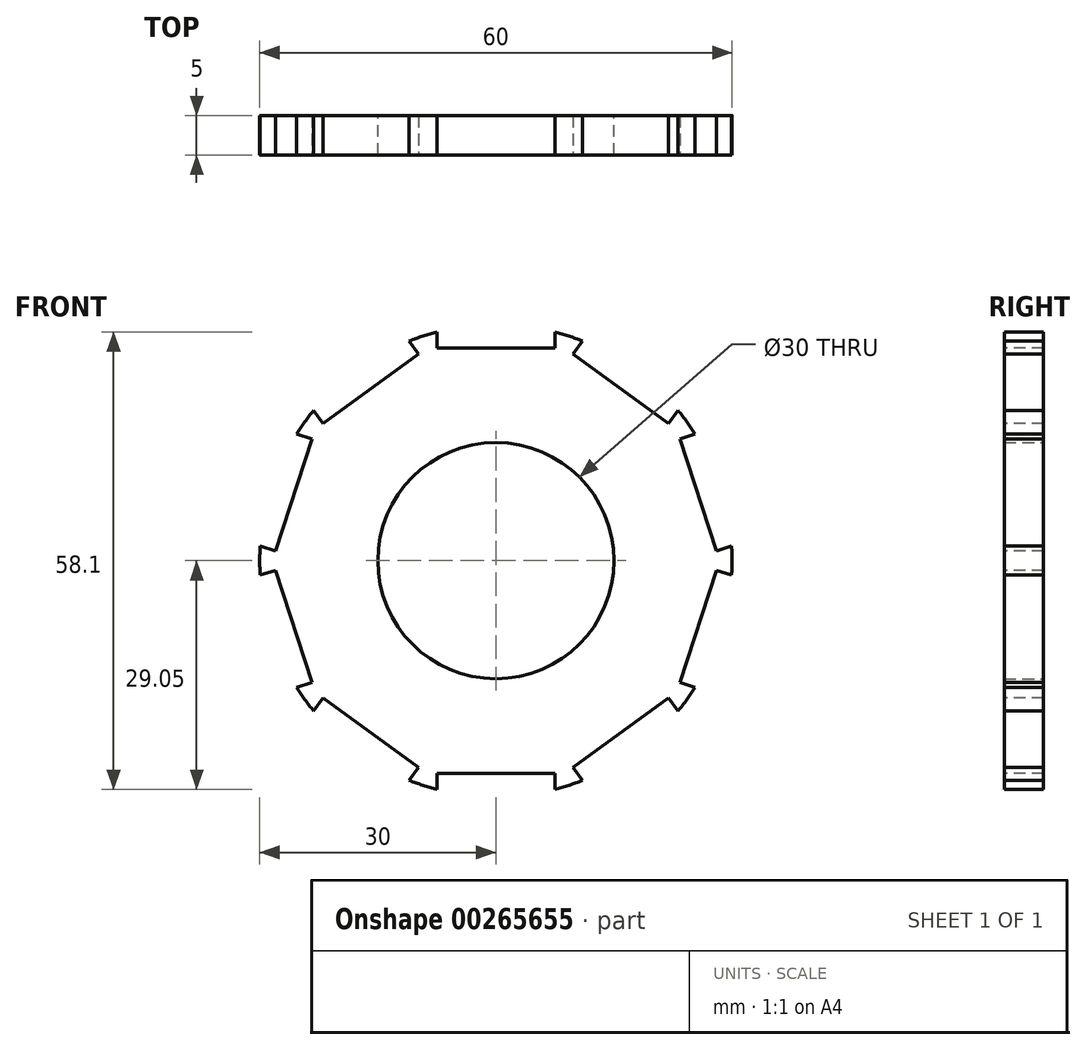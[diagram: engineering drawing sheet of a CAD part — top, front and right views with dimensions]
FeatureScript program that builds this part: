
annotation { "Feature Type Name" : "Feature", "Feature Type Description" : "" }
export const myFeature = defineFeature(function(context is Context, id is Id, definition is map)
    precondition{}
    {
        {
            var Q0;
            Q0=qCreatedBy(makeId("Front.planeOp"),FACE);
            var sketch = newSketch(context, id + "F0", { "sketchPlane" : qUnion([Q0])});
            skCircle(sketch, "E0", {"center": v(0, 0) * mm, "radius": 30 * mm});
            skCircle(sketch, "E1", {"center": v(0, 0) * mm, "radius": 15 * mm});
            skSolve(sketch);
        }
        {
            var Q0;
            Q0 = qSketchRegion(id + "F0", true);
            extrude(context, id + "F1", {"entities" : qUnion([Q0]), "depth" : 5 * mm});
        }
        {
            var Q0;
            Q0=makeQuery(id+"F1.opExtrude","CAP_FACE",FACE,{"disambiguationData":[OSD([sQuery(id+"F0.wireOp",EDGE,"E0"),sQuery(id+"F0.wireOp",EDGE,"E1")])],"isStart":false});
            var sketch = newSketch(context, id + "F3", { "sketchPlane" : qUnion([Q0])});
            skLineSegment(sketch, "E2", {"start": v(0, 30) * mm, "end": v(0, 27) * mm});
            skLineSegment(sketch, "E3", {"start": v(0, 27) * mm, "end": v(-7.5, 27) * mm});
            skLineSegment(sketch, "E4", {"start": v(-7.5, 27) * mm, "end": v(-7.5, 29.05) * mm});
            skLineSegment(sketch, "E5.MirrorCS", {"start": v(0, 27) * mm, "end": v(7.5, 27) * mm});
            skLineSegment(sketch, "E6.MirrorCS", {"start": v(7.5, 27) * mm, "end": v(7.5, 29.05) * mm});
            skArc(sketch, "E7", {"start": v(7.5, 29.05) * mm, "mid": v(0, 30) * mm, "end": v(-7.5, 29.05) * mm});
            skLineSegment(sketch, "E8.1.0", {"start": v(-15.87, 21.84) * mm, "end": v(-21.94, 17.44) * mm});
            skLineSegment(sketch, "E8.1.1", {"start": v(-15.87, 21.84) * mm, "end": v(-9.8, 26.25) * mm});
            skArc(sketch, "E8.1.2", {"start": v(-11, 27.9) * mm, "mid": v(-17.63, 24.27) * mm, "end": v(-23.14, 19.1) * mm});
            skLineSegment(sketch, "E8.1.3", {"start": v(-21.94, 17.44) * mm, "end": v(-23.14, 19.1) * mm});
            skLineSegment(sketch, "E8.1.4", {"start": v(-9.8, 26.25) * mm, "end": v(-11, 27.9) * mm});
            skLineSegment(sketch, "E8.1.5", {"start": v(-17.63, 24.27) * mm, "end": v(-15.87, 21.84) * mm});
            skLineSegment(sketch, "E8.2.0", {"start": v(-25.68, 8.34) * mm, "end": v(-28, 1.21) * mm});
            skLineSegment(sketch, "E8.2.1", {"start": v(-25.68, 8.34) * mm, "end": v(-23.36, 15.48) * mm});
            skArc(sketch, "E8.2.2", {"start": v(-25.3, 16.1) * mm, "mid": v(-28.53, 9.27) * mm, "end": v(-29.94, 1.84) * mm});
            skLineSegment(sketch, "E8.2.3", {"start": v(-28, 1.21) * mm, "end": v(-29.94, 1.84) * mm});
            skLineSegment(sketch, "E8.2.4", {"start": v(-23.36, 15.48) * mm, "end": v(-25.3, 16.1) * mm});
            skLineSegment(sketch, "E8.2.5", {"start": v(-28.53, 9.27) * mm, "end": v(-25.68, 8.34) * mm});
            skLineSegment(sketch, "E8.3.0", {"start": v(-25.68, -8.34) * mm, "end": v(-23.36, -15.48) * mm});
            skLineSegment(sketch, "E8.3.1", {"start": v(-25.68, -8.34) * mm, "end": v(-28, -1.21) * mm});
            skArc(sketch, "E8.3.2", {"start": v(-29.94, -1.84) * mm, "mid": v(-28.53, -9.27) * mm, "end": v(-25.3, -16.1) * mm});
            skLineSegment(sketch, "E8.3.3", {"start": v(-23.36, -15.48) * mm, "end": v(-25.3, -16.1) * mm});
            skLineSegment(sketch, "E8.3.4", {"start": v(-28, -1.21) * mm, "end": v(-29.94, -1.84) * mm});
            skLineSegment(sketch, "E8.3.5", {"start": v(-28.53, -9.27) * mm, "end": v(-25.68, -8.34) * mm});
            skLineSegment(sketch, "E8.4.0", {"start": v(-15.87, -21.84) * mm, "end": v(-9.8, -26.25) * mm});
            skLineSegment(sketch, "E8.4.1", {"start": v(-15.87, -21.84) * mm, "end": v(-21.94, -17.44) * mm});
            skArc(sketch, "E8.4.2", {"start": v(-23.14, -19.1) * mm, "mid": v(-17.63, -24.27) * mm, "end": v(-11, -27.9) * mm});
            skLineSegment(sketch, "E8.4.3", {"start": v(-9.8, -26.25) * mm, "end": v(-11, -27.9) * mm});
            skLineSegment(sketch, "E8.4.4", {"start": v(-21.94, -17.44) * mm, "end": v(-23.14, -19.1) * mm});
            skLineSegment(sketch, "E8.4.5", {"start": v(-17.63, -24.27) * mm, "end": v(-15.87, -21.84) * mm});
            skLineSegment(sketch, "E8.5.0", {"start": v(0, -27) * mm, "end": v(7.5, -27) * mm});
            skLineSegment(sketch, "E8.5.1", {"start": v(0, -27) * mm, "end": v(-7.5, -27) * mm});
            skArc(sketch, "E8.5.2", {"start": v(-7.5, -29.05) * mm, "mid": v(0, -30) * mm, "end": v(7.5, -29.05) * mm});
            skLineSegment(sketch, "E8.5.3", {"start": v(7.5, -27) * mm, "end": v(7.5, -29.05) * mm});
            skLineSegment(sketch, "E8.5.4", {"start": v(-7.5, -27) * mm, "end": v(-7.5, -29.05) * mm});
            skLineSegment(sketch, "E8.5.5", {"start": v(0, -30) * mm, "end": v(0, -27) * mm});
            skLineSegment(sketch, "E8.6.0", {"start": v(15.87, -21.84) * mm, "end": v(21.94, -17.44) * mm});
            skLineSegment(sketch, "E8.6.1", {"start": v(15.87, -21.84) * mm, "end": v(9.8, -26.25) * mm});
            skArc(sketch, "E8.6.2", {"start": v(11, -27.9) * mm, "mid": v(17.63, -24.27) * mm, "end": v(23.14, -19.1) * mm});
            skLineSegment(sketch, "E8.6.3", {"start": v(21.94, -17.44) * mm, "end": v(23.14, -19.1) * mm});
            skLineSegment(sketch, "E8.6.4", {"start": v(9.8, -26.25) * mm, "end": v(11, -27.9) * mm});
            skLineSegment(sketch, "E8.6.5", {"start": v(17.63, -24.27) * mm, "end": v(15.87, -21.84) * mm});
            skLineSegment(sketch, "E8.7.0", {"start": v(25.68, -8.34) * mm, "end": v(28, -1.21) * mm});
            skLineSegment(sketch, "E8.7.1", {"start": v(25.68, -8.34) * mm, "end": v(23.36, -15.48) * mm});
            skArc(sketch, "E8.7.2", {"start": v(25.3, -16.1) * mm, "mid": v(28.53, -9.27) * mm, "end": v(29.94, -1.84) * mm});
            skLineSegment(sketch, "E8.7.3", {"start": v(28, -1.21) * mm, "end": v(29.94, -1.84) * mm});
            skLineSegment(sketch, "E8.7.4", {"start": v(23.36, -15.48) * mm, "end": v(25.3, -16.1) * mm});
            skLineSegment(sketch, "E8.7.5", {"start": v(28.53, -9.27) * mm, "end": v(25.68, -8.34) * mm});
            skLineSegment(sketch, "E8.8.0", {"start": v(25.68, 8.34) * mm, "end": v(23.36, 15.48) * mm});
            skLineSegment(sketch, "E8.8.1", {"start": v(25.68, 8.34) * mm, "end": v(28, 1.21) * mm});
            skArc(sketch, "E8.8.2", {"start": v(29.94, 1.84) * mm, "mid": v(28.53, 9.27) * mm, "end": v(25.3, 16.1) * mm});
            skLineSegment(sketch, "E8.8.3", {"start": v(23.36, 15.48) * mm, "end": v(25.3, 16.1) * mm});
            skLineSegment(sketch, "E8.8.4", {"start": v(28, 1.21) * mm, "end": v(29.94, 1.84) * mm});
            skLineSegment(sketch, "E8.8.5", {"start": v(28.53, 9.27) * mm, "end": v(25.68, 8.34) * mm});
            skLineSegment(sketch, "E8.9.0", {"start": v(15.87, 21.84) * mm, "end": v(9.8, 26.25) * mm});
            skLineSegment(sketch, "E8.9.1", {"start": v(15.87, 21.84) * mm, "end": v(21.94, 17.44) * mm});
            skArc(sketch, "E8.9.2", {"start": v(23.14, 19.1) * mm, "mid": v(17.63, 24.27) * mm, "end": v(11, 27.9) * mm});
            skLineSegment(sketch, "E8.9.3", {"start": v(9.8, 26.25) * mm, "end": v(11, 27.9) * mm});
            skLineSegment(sketch, "E8.9.4", {"start": v(21.94, 17.44) * mm, "end": v(23.14, 19.1) * mm});
            skLineSegment(sketch, "E8.9.5", {"start": v(17.63, 24.27) * mm, "end": v(15.87, 21.84) * mm});
            skSolve(sketch);
        }
        {
            var Q0;
            Q0 = qSketchRegion(id + "F3", true);
            extrude(context, id + "F2", {"entities" : qUnion([Q0]), "operationType" : NewBodyOperationType.REMOVE, "oppositeDirection" : true, "depth" : 25 * mm});
        }
    });
